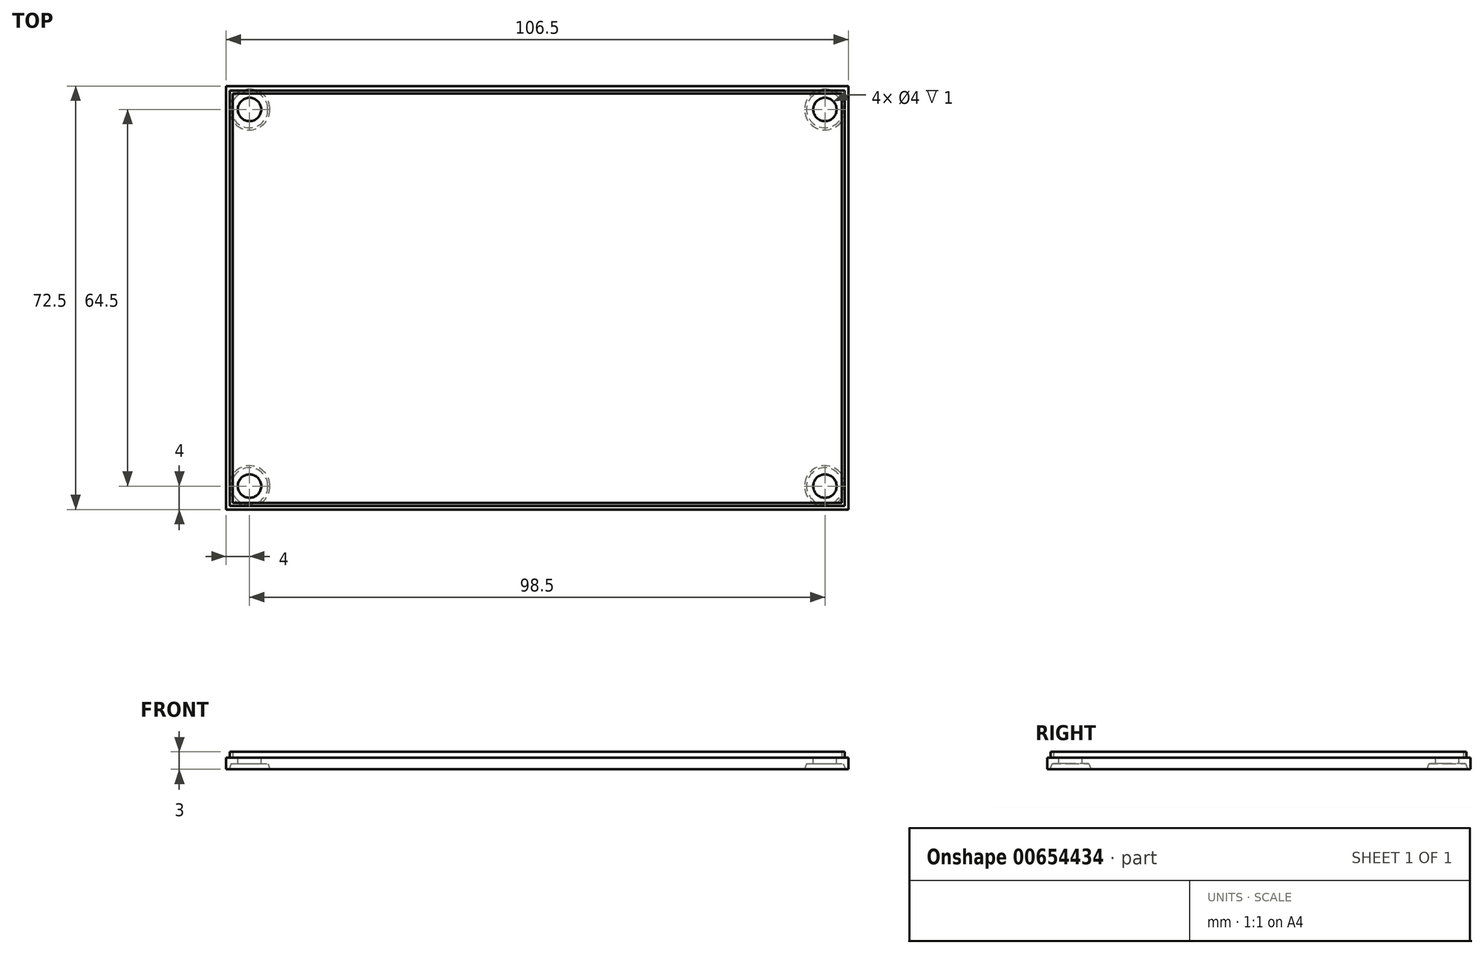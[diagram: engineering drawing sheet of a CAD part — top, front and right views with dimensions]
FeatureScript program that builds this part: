
annotation { "Feature Type Name" : "Feature", "Feature Type Description" : "" }
export const myFeature = defineFeature(function(context is Context, id is Id, definition is map)
    precondition{}
    {
        {
            var Q0;
            Q0=qCreatedBy(makeId("Top.planeOp"),FACE);
            var sketch = newSketch(context, id + "F0", { "sketchPlane" : qUnion([Q0])});
            skLineSegment(sketch, "E0.bottom", {"start": v(0, 0) * mm, "end": v(-106.5, 0) * mm});
            skLineSegment(sketch, "E0.top", {"start": v(0, 72.5) * mm, "end": v(-106.5, 72.5) * mm});
            skLineSegment(sketch, "E0.left", {"start": v(0, 0) * mm, "end": v(0, 72.5) * mm});
            skLineSegment(sketch, "E0.right", {"start": v(-106.5, 0) * mm, "end": v(-106.5, 72.5) * mm});
            skSolve(sketch);
        }
        {
            var Q0;
            Q0=qSketchRegion(id+"F0",true);
            extrude(context, id + "F1", {"entities" : qUnion([Q0]), "depth" : 2 * mm, "offsetDistance" : 25 * mm});
        }
        {
            var Q0;
            {var subQ0=sQuery(id+"F0.wireOp",EDGE,"E0.left");var subQ1=sQuery(id+"F0.wireOp",EDGE,"E0.top");var subQ2=sQuery(id+"F0.wireOp",EDGE,"E0.right");var subQ3=sQuery(id+"F0.wireOp",EDGE,"E0.bottom");Q0=makeQuery(id+"FumT0qbEayIIpZh_1.boolean.opBoolean","SPLIT",FACE,{"disambiguationData":[TD([makeQuery(id+"F1.opExtrude","SWEPT_FACE",FACE,{"disambiguationData":[OSD([subQ3])]})])],"derivedFrom":makeQuery(id+"F1.opExtrude","CAP_FACE",FACE,{"disambiguationData":[OSD([subQ3,subQ1,subQ0,subQ2])],"isStart":false})});}
            var sketch = newSketch(context, id + "F2", { "sketchPlane" : qUnion([Q0])});
            skCircle(sketch, "E1", {"center": v(-102.5, 68.5) * mm, "radius": 2 * mm});
            skLineSegment(sketch, "E2", {"start": v(-53.25, 72.5) * mm, "end": v(-53.25, 0) * mm, "construction": true});
            skLineSegment(sketch, "E3", {"start": v(-106.5, 36.25) * mm, "end": v(0, 36.25) * mm, "construction": true});
            skCircle(sketch, "E4.MirrorC", {"center": v(-4, 68.5) * mm, "radius": 2 * mm});
            skCircle(sketch, "E5.MirrorC", {"center": v(-4, 4) * mm, "radius": 2 * mm});
            skCircle(sketch, "E6.MirrorC", {"center": v(-102.5, 4) * mm, "radius": 2 * mm});
            skSolve(sketch);
        }
        {
            var Q0;
            Q0 = qSketchRegion(id + "F2", true);
            extrude(context, id + "F3", {"entities" : qUnion([Q0]), "operationType" : NewBodyOperationType.REMOVE, "endBound" : BoundingType.UP_TO_NEXT, "oppositeDirection" : true, "depth" : 25 * mm, "offsetDistance" : 25 * mm});
        }
        {
            var Q0;
            Q0=makeQuery(id+"F1.opExtrude","CAP_FACE",FACE,{"disambiguationData":[OSD([sQuery(id+"F0.wireOp",EDGE,"E0.bottom"),sQuery(id+"F0.wireOp",EDGE,"E0.top"),sQuery(id+"F0.wireOp",EDGE,"E0.left"),sQuery(id+"F0.wireOp",EDGE,"E0.right")])],"isStart":true});
            var sketch = newSketch(context, id + "F4", { "sketchPlane" : qUnion([Q0])});
            skCircle(sketch, "E7", {"center": v(-102.5, -4) * mm, "radius": 3.5 * mm});
            skLineSegment(sketch, "E8", {"start": v(-53.25, 0) * mm, "end": v(-53.25, -72.5) * mm, "construction": true});
            skLineSegment(sketch, "E9", {"start": v(-106.5, -36.25) * mm, "end": v(0, -36.25) * mm, "construction": true});
            skCircle(sketch, "E10.MirrorC", {"center": v(-4, -4) * mm, "radius": 3.5 * mm});
            skCircle(sketch, "E11.MirrorC", {"center": v(-102.5, -68.5) * mm, "radius": 3.5 * mm});
            skCircle(sketch, "E12.MirrorC", {"center": v(-4, -68.5) * mm, "radius": 3.5 * mm});
            skSolve(sketch);
        }
        {
            var Q0;
            Q0 = qSketchRegion(id + "F4", true);
            extrude(context, id + "F5", {"entities" : qUnion([Q0]), "operationType" : NewBodyOperationType.REMOVE, "oppositeDirection" : true, "depth" : 1 * mm, "offsetDistance" : 25 * mm, "hasDraft" : true, "draftAngle" : 20 * degree, "draftPullDirection" : true});
        }
        {
            var Q0;
            {var subQ0=sQuery(id+"F0.wireOp",EDGE,"E0.left");var subQ1=sQuery(id+"F0.wireOp",EDGE,"E0.top");var subQ2=sQuery(id+"F0.wireOp",EDGE,"E0.right");var subQ3=sQuery(id+"F0.wireOp",EDGE,"E0.bottom");Q0=makeQuery(id+"FumT0qbEayIIpZh_1.boolean.opBoolean","SPLIT",FACE,{"disambiguationData":[TD([makeQuery(id+"F1.opExtrude","SWEPT_FACE",FACE,{"disambiguationData":[OSD([subQ3])]})])],"derivedFrom":makeQuery(id+"F1.opExtrude","CAP_FACE",FACE,{"disambiguationData":[OSD([subQ3,subQ1,subQ0,subQ2])],"isStart":false})});}
            var sketch = newSketch(context, id + "F6", { "sketchPlane" : qUnion([Q0])});
            skLineSegment(sketch, "E13.bottom", {"start": v(-105.38, 71.25) * mm, "end": v(-1.13, 71.25) * mm});
            skLineSegment(sketch, "E13.top", {"start": v(-105.38, 1.13) * mm, "end": v(-1.13, 1.13) * mm});
            skLineSegment(sketch, "E13.left", {"start": v(-105.38, 71.25) * mm, "end": v(-105.38, 1.13) * mm});
            skLineSegment(sketch, "E13.right", {"start": v(-1.13, 71.25) * mm, "end": v(-1.12, 1.13) * mm});
            skLineSegment(sketch, "E14.0", {"start": v(-105.88, 71.75) * mm, "end": v(-0.63, 71.75) * mm});
            skLineSegment(sketch, "E14.1", {"start": v(-105.88, 71.75) * mm, "end": v(-105.88, 0.63) * mm});
            skLineSegment(sketch, "E14.2", {"start": v(-105.88, 0.62) * mm, "end": v(-0.63, 0.62) * mm});
            skLineSegment(sketch, "E14.3", {"start": v(-0.63, 71.75) * mm, "end": v(-0.62, 0.63) * mm});
            skSolve(sketch);
        }
        {
            var Q0;
            Q0 = qSketchRegion(id + "F6", true);
            extrude(context, id + "F7", {"entities" : qUnion([Q0]), "operationType" : NewBodyOperationType.ADD, "depth" : 1 * mm, "offsetDistance" : 25 * mm});
        }
    });
